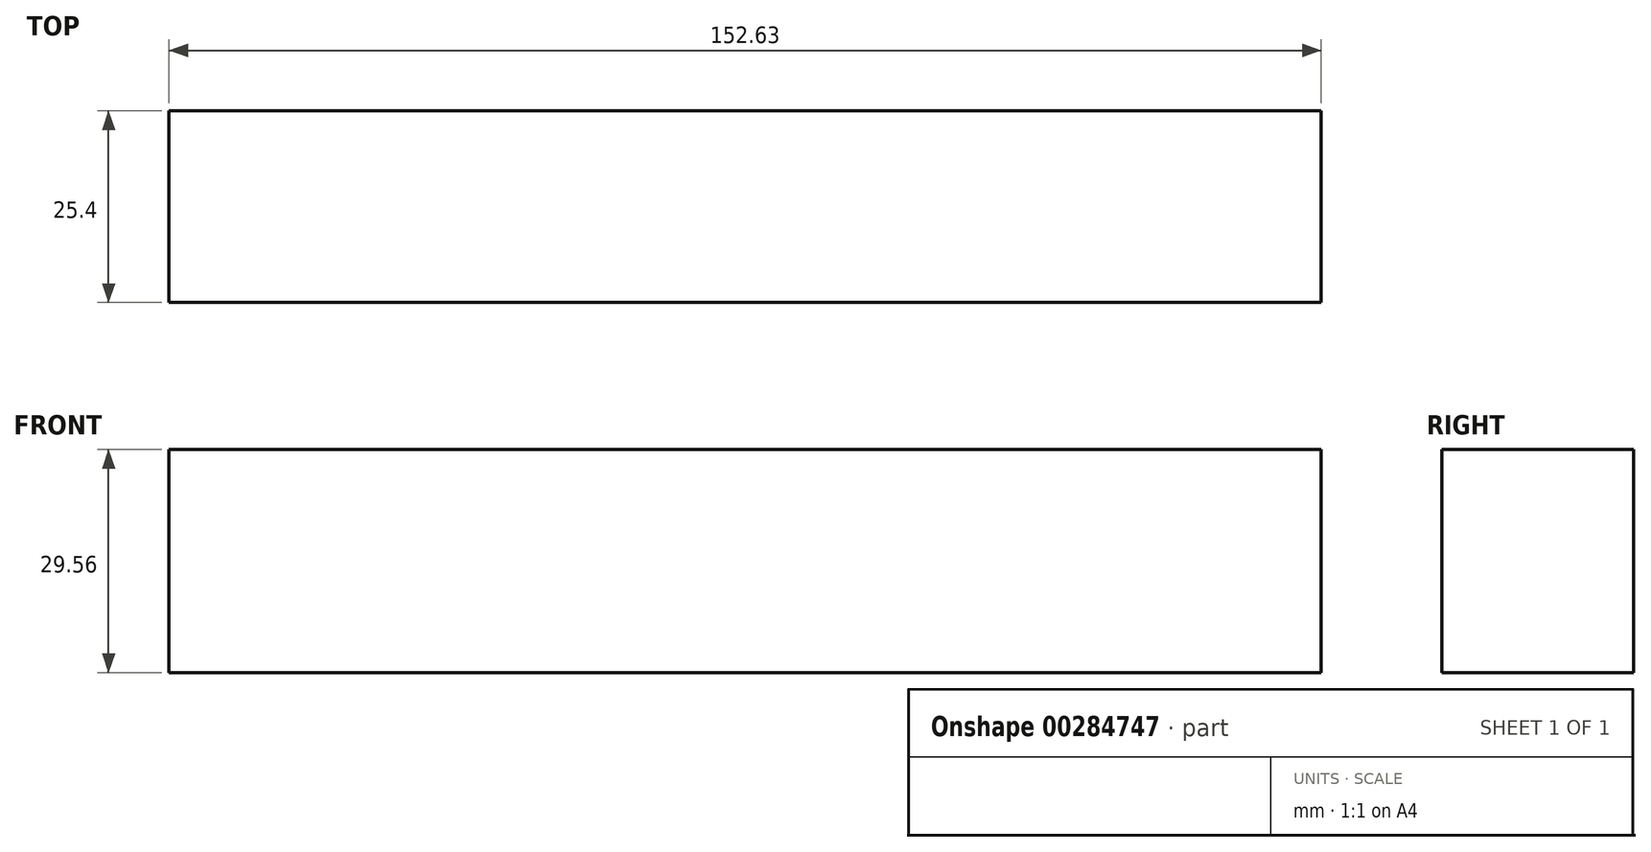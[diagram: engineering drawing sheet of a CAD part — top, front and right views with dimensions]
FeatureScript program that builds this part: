
annotation { "Feature Type Name" : "Feature", "Feature Type Description" : "" }
export const myFeature = defineFeature(function(context is Context, id is Id, definition is map)
    precondition{}
    {
        {
            var Q0;
            Q0=qCreatedBy(makeId("Front.planeOp"),FACE);
            var sketch = newSketch(context, id + "F0", { "sketchPlane" : qUnion([Q0])});
            skLineSegment(sketch, "E0.bottom", {"start": v(0, 0) * mm, "end": v(76.68, 0) * mm});
            skLineSegment(sketch, "E0.top", {"start": v(0, 16) * mm, "end": v(76.68, 16) * mm});
            skLineSegment(sketch, "E0.left", {"start": v(0, 0) * mm, "end": v(0, 16) * mm});
            skLineSegment(sketch, "E0.right", {"start": v(76.68, 0) * mm, "end": v(76.68, 16) * mm});
            skLineSegment(sketch, "E1.bottom", {"start": v(0, 0) * mm, "end": v(-75.95, 0) * mm});
            skLineSegment(sketch, "E1.top", {"start": v(0, 16) * mm, "end": v(-75.95, 16) * mm});
            skLineSegment(sketch, "E1.right", {"start": v(-75.95, 0) * mm, "end": v(-75.95, 16) * mm});
            skLineSegment(sketch, "E2.top", {"start": v(0, -13.57) * mm, "end": v(76.68, -13.57) * mm});
            skLineSegment(sketch, "E2.left", {"start": v(0, 0) * mm, "end": v(0, -13.57) * mm});
            skLineSegment(sketch, "E2.right", {"start": v(76.68, 0) * mm, "end": v(76.68, -13.57) * mm});
            skLineSegment(sketch, "E3.top", {"start": v(0, -13.57) * mm, "end": v(-75.95, -13.57) * mm});
            skLineSegment(sketch, "E3.right", {"start": v(-75.95, 0) * mm, "end": v(-75.95, -13.57) * mm});
            skSolve(sketch);
        }
        {
            var Q0;
            Q0=makeQuery(id+"F0.imprint","IMPRINT",FACE,{"disambiguationData":[TD([[makeQuery(id+"F0.imprint","IMPRINT",EDGE,{"derivedFrom":sQuery(id+"F0.wireOp",EDGE,"E0.bottom")}),-1.0]])]});
            var Q1;
            Q1=makeQuery(id+"F0.imprint","IMPRINT",FACE,{"disambiguationData":[TD([[makeQuery(id+"F0.imprint","IMPRINT",EDGE,{"derivedFrom":sQuery(id+"F0.wireOp",EDGE,"E0.top")}),-1.0]])]});
            var Q2;
            Q2=makeQuery(id+"F0.imprint","IMPRINT",FACE,{"disambiguationData":[TD([[makeQuery(id+"F0.imprint","IMPRINT",EDGE,{"derivedFrom":sQuery(id+"F0.wireOp",EDGE,"E1.bottom")}),1.0]])]});
            var Q3;
            Q3=makeQuery(id+"F0.imprint","IMPRINT",FACE,{"disambiguationData":[TD([[makeQuery(id+"F0.imprint","IMPRINT",EDGE,{"derivedFrom":sQuery(id+"F0.wireOp",EDGE,"E1.top")}),1.0]])]});
            extrude(context, id + "F1", {"entities" : qUnion([Q0, Q1, Q2, Q3]), "depth" : 25.4 * mm});
        }
    });
